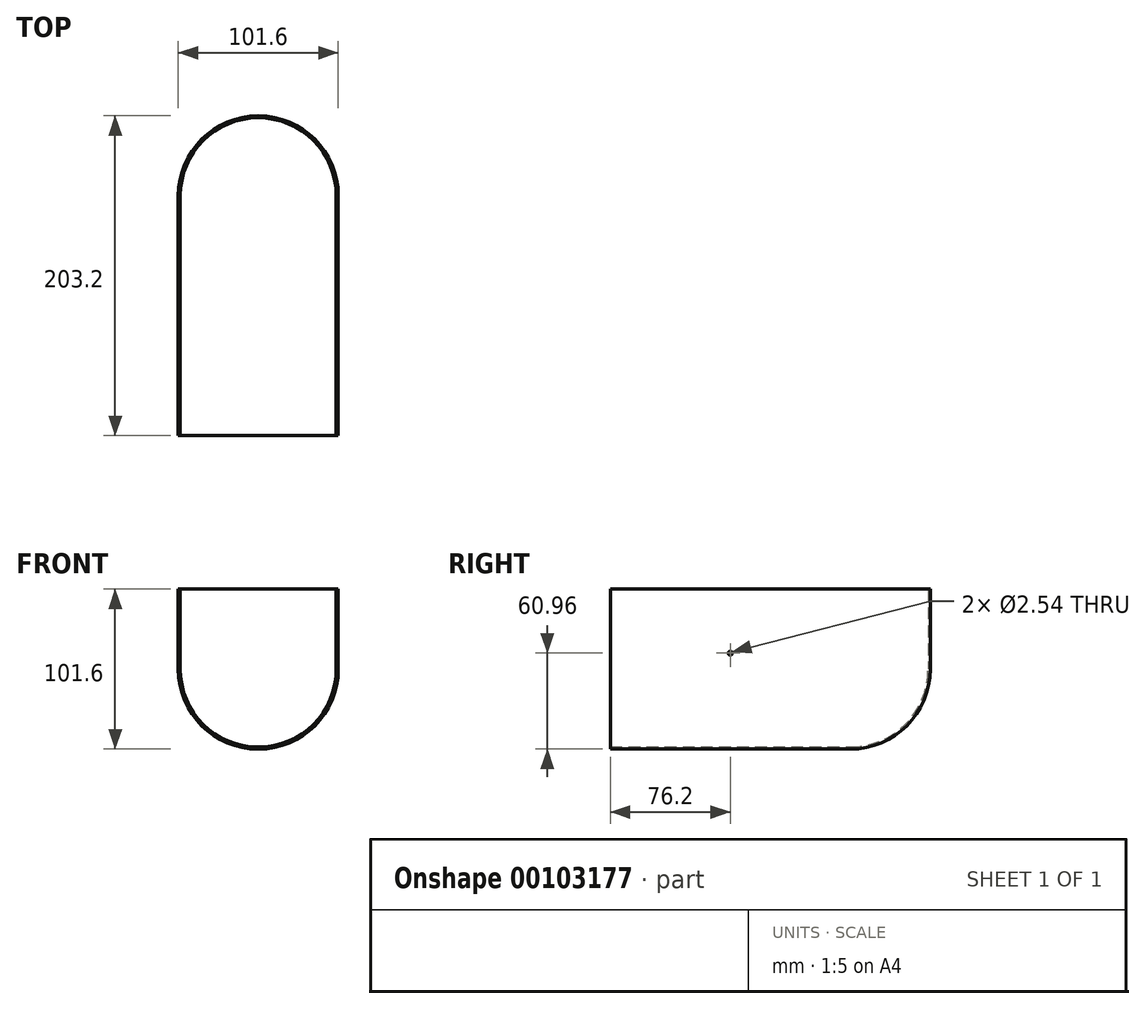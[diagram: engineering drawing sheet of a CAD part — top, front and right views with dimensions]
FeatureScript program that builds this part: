
annotation { "Feature Type Name" : "Feature", "Feature Type Description" : "" }
export const myFeature = defineFeature(function(context is Context, id is Id, definition is map)
    precondition{}
    {
        {
            var Q0;
            Q0=qCreatedBy(makeId("Top.planeOp"),FACE);
            var sketch = newSketch(context, id + "F0", { "sketchPlane" : qUnion([Q0])});
            skLineSegment(sketch, "E0.bottom", {"start": v(0, -76.2) * mm, "end": v(-50.8, -76.2) * mm});
            skLineSegment(sketch, "E0.top", {"start": v(-49.53, 76.2) * mm, "end": v(-50.8, 76.2) * mm});
            skLineSegment(sketch, "E0.right", {"start": v(-50.8, -76.2) * mm, "end": v(-50.8, 76.2) * mm});
            skPoint(sketch, "E0.middle", {"position": v(0, 0) * mm});
            skLineSegment(sketch, "E1", {"start": v(0, 76.2) * mm, "end": v(0, 0) * mm});
            skPoint(sketch, "E0.left.end.orphan", {"position": v(50.8, 76.2) * mm});
            skPoint(sketch, "E2.orphan", {"position": v(50.8, -76.2) * mm});
            skArc(sketch, "E3", {"start": v(0, 127) * mm, "mid": v(-35.92, 112.12) * mm, "end": v(-50.8, 76.2) * mm});
            skLineSegment(sketch, "E4", {"start": v(0, 125.73) * mm, "end": v(0, 127) * mm});
            skArc(sketch, "E5", {"start": v(0, 125.73) * mm, "mid": v(-35.02, 111.22) * mm, "end": v(-49.53, 76.2) * mm});
            skLineSegment(sketch, "E6", {"start": v(-49.53, 76.2) * mm, "end": v(-49.53, -76.2) * mm});
            skSolve(sketch);
        }
        {
            var Q0;
            Q0 = qSketchRegion(id + "F0", true);
            var Q1;
            Q1=makeQuery(id+"F0.imprint","IMPRINT",FACE,{"disambiguationData":[TD([[makeQuery(id+"F0.imprint","IMPRINT",EDGE,{"derivedFrom":sQuery(id+"F0.wireOp",EDGE,"E0.top")}),1.0]])]});
            var Q2;
            Q2=sQuery(id+"F0.wireOp",EDGE,"E1");
            revolve(context, id + "F1", {"entities" : qUnion([Q0, Q1]), "axis" : qUnion([Q2]), "revolveType" : RevolveType.ONE_DIRECTION, "angle" : 180 * degree});
        }
        {
            var Q0;
            Q0=makeQuery(id+"F1.opRevolve","CAP_FACE",FACE,{"disambiguationData":[OSD([sQuery(id+"F0.wireOp",EDGE,"E0.bottom"),sQuery(id+"F0.wireOp",EDGE,"E0.right"),sQuery(id+"F0.wireOp",EDGE,"E3"),sQuery(id+"F0.wireOp",EDGE,"E4"),sQuery(id+"F0.wireOp",EDGE,"E5"),sQuery(id+"F0.wireOp",EDGE,"E6")])],"isStart":false});
            extrude(context, id + "F2", {"entities" : qUnion([Q0]), "operationType" : NewBodyOperationType.ADD, "depth" : 50.8 * mm});
        }
        {
            var Q0;
            {var subQ0=sQuery(id+"F0.wireOp",EDGE,"E0.right");Q0=makeQuery(id+"F2.opExtrude","SWEPT_FACE",FACE,{"disambiguationData":[OSD([subQ0]),TDD([makeQuery(id+"F1.opRevolve","CAP_EDGE",EDGE,{"disambiguationData":[OSD([subQ0])],"isStart":true})])]});}
            var sketch = newSketch(context, id + "F3", { "sketchPlane" : qUnion([Q0])});
            skCircle(sketch, "E7", {"center": v(0, 10.16) * mm, "radius": 1.27 * mm});
            skSolve(sketch);
        }
        {
            var Q0;
            Q0=makeQuery(id+"F3.imprint","IMPRINT",FACE,{"disambiguationData":[TD([[makeQuery(id+"F3.imprint","IMPRINT",EDGE,{"derivedFrom":sQuery(id+"F3.wireOp",EDGE,"E7")}),1.0]])]});
            extrude(context, id + "F4", {"entities" : qUnion([Q0]), "operationType" : NewBodyOperationType.REMOVE, "oppositeDirection" : true, "depth" : 25.4 * mm});
        }
        {
            var Q0;
            {var subQ0=sQuery(id+"F0.wireOp",EDGE,"E0.right");Q0=makeQuery(id+"F2.opExtrude","SWEPT_FACE",FACE,{"disambiguationData":[OSD([subQ0]),TDD([makeQuery(id+"F1.opRevolve","CAP_EDGE",EDGE,{"disambiguationData":[OSD([subQ0])],"isStart":false})])]});}
            var sketch = newSketch(context, id + "F5", { "sketchPlane" : qUnion([Q0])});
            skCircle(sketch, "E8", {"center": v(0, 10.16) * mm, "radius": 1.27 * mm});
            skSolve(sketch);
        }
        {
            var Q0;
            Q0 = qSketchRegion(id + "F5", true);
            var Q1;
            Q1=makeQuery(id+"F5.imprint","IMPRINT",FACE,{"disambiguationData":[TD([[makeQuery(id+"F5.imprint","IMPRINT",EDGE,{"derivedFrom":sQuery(id+"F5.wireOp",EDGE,"E8")}),1.0]])]});
            extrude(context, id + "F6", {"entities" : qUnion([Q0, Q1]), "operationType" : NewBodyOperationType.REMOVE, "oppositeDirection" : true, "depth" : 25.4 * mm});
        }
    });
